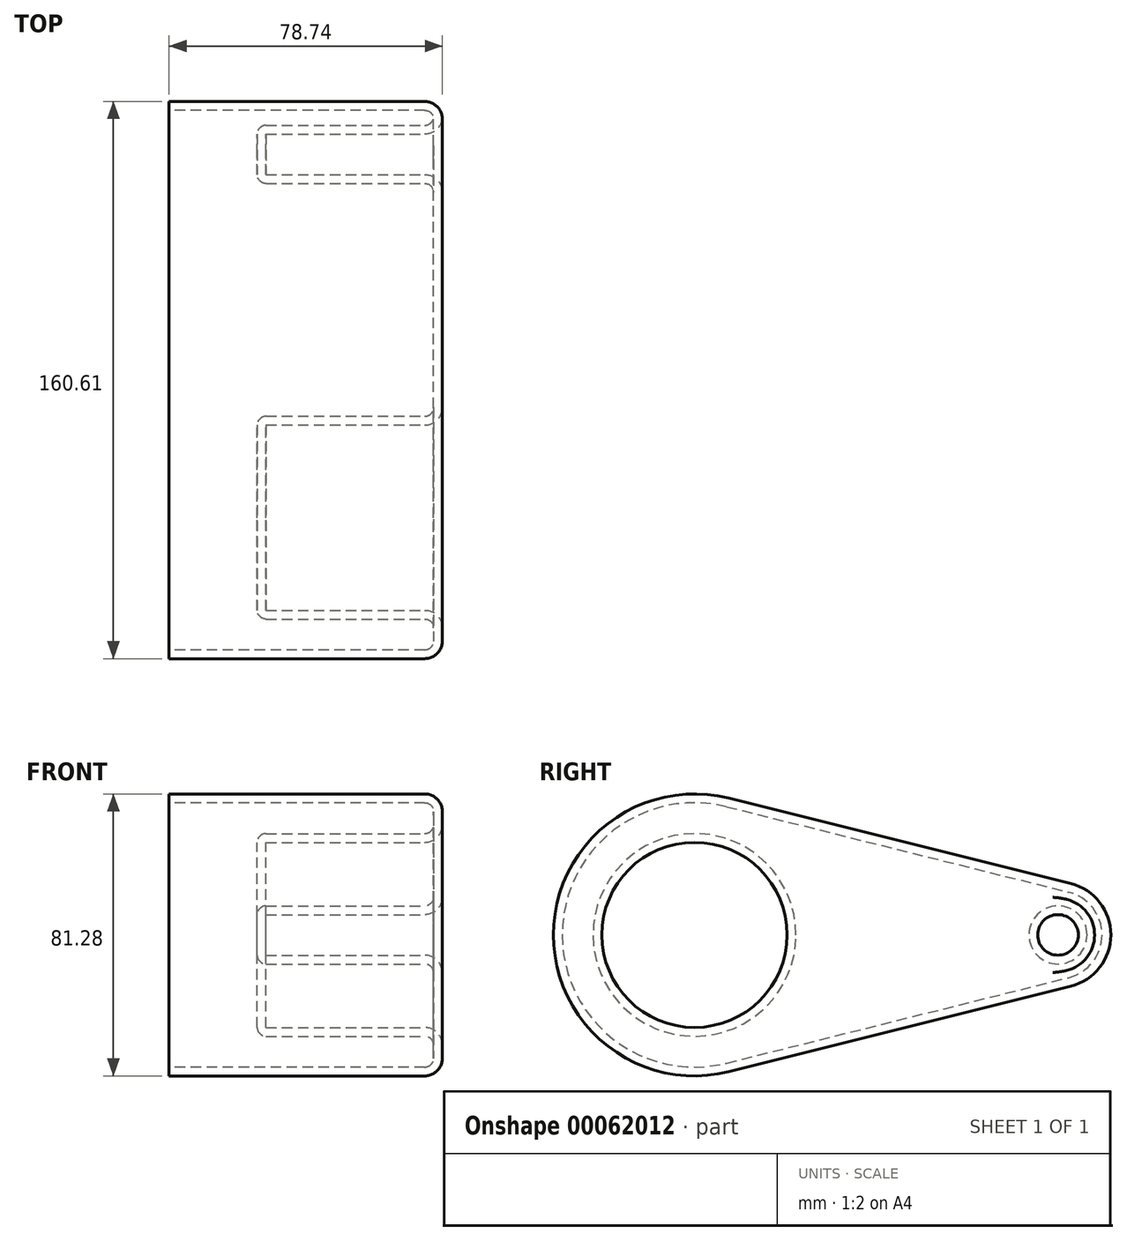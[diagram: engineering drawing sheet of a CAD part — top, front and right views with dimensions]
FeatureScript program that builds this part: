
annotation { "Feature Type Name" : "Feature", "Feature Type Description" : "" }
export const myFeature = defineFeature(function(context is Context, id is Id, definition is map)
    precondition{}
    {
        {
            var Q0;
            Q0=qCreatedBy(makeId("Right.planeOp"),FACE);
            var sketch = newSketch(context, id + "F3", { "sketchPlane" : qUnion([Q0])});
            skCircle(sketch, "E0", {"center": v(0, 0) * mm, "radius": 38.1 * mm});
            skCircle(sketch, "E1", {"center": v(104.73, 0) * mm, "radius": 12.7 * mm});
            skLineSegment(sketch, "E2", {"start": v(9.24, 36.96) * mm, "end": v(107.8, 12.32) * mm});
            skLineSegment(sketch, "E3", {"start": v(64.15, 21.02) * mm, "end": v(64.15, 21.02) * mm});
            skLineSegment(sketch, "E4", {"start": v(9.24, -36.96) * mm, "end": v(107.8, -12.32) * mm});
            skSolve(sketch);
        }
        {
            var Q0;
            Q0 = qSketchRegion(id + "F3", true);
            extrude(context, id + "F0", {"entities" : qUnion([Q0]), "depth" : 76.2 * mm});
        }
        {
            var Q0;
            Q0=makeQuery(id+"F0.opExtrude","CAP_FACE",FACE,{"disambiguationData":[OSD([sQuery(id+"F3.wireOp",EDGE,"E0"),sQuery(id+"F3.wireOp",EDGE,"E1"),sQuery(id+"F3.wireOp",EDGE,"E2"),sQuery(id+"F3.wireOp",EDGE,"E4")])],"isStart":false});
            var sketch = newSketch(context, id + "F4", { "sketchPlane" : qUnion([Q0])});
            skCircle(sketch, "E5", {"center": v(0, 0) * mm, "radius": 29.22 * mm});
            skCircle(sketch, "E6", {"center": v(104.73, 0) * mm, "radius": 8.38 * mm});
            skSolve(sketch);
        }
        {
            var Q0;
            Q0 = qSketchRegion(id + "F4", true);
            extrude(context, id + "F5", {"entities" : qUnion([Q0]), "operationType" : NewBodyOperationType.REMOVE, "oppositeDirection" : true, "depth" : 50.8 * mm});
        }
        {
            var Q0;
            Q0=makeQuery(id+"F0.opExtrude","CAP_FACE",FACE,{"disambiguationData":[OSD([sQuery(id+"F3.wireOp",EDGE,"E0"),sQuery(id+"F3.wireOp",EDGE,"E1"),sQuery(id+"F3.wireOp",EDGE,"E2"),sQuery(id+"F3.wireOp",EDGE,"E4")])],"isStart":false});
            var Q1;
            Q1=makeQuery(id+"F5.boolean.opBoolean","COPY",FACE,{"derivedFrom":makeQuery(id+"F5.opExtrude","CAP_FACE",FACE,{"disambiguationData":[OSD([sQuery(id+"F4.wireOp",EDGE,"E5")])],"isStart":false})});
            var Q2;
            Q2=makeQuery(id+"F5.boolean.opBoolean","COPY",FACE,{"derivedFrom":makeQuery(id+"F5.opExtrude","CAP_FACE",FACE,{"disambiguationData":[OSD([sQuery(id+"F4.wireOp",EDGE,"E6")])],"isStart":false})});
            fillet(context, id + "F1", {"entities" : qUnion([Q0, Q1, Q2]), "radius" : 2.54 * mm, "tangentPropagation" : true, "allowEdgeOverflow" : false});
        }
        {
            var Q0;
            Q0=makeQuery(id+"F0.opExtrude","CAP_FACE",FACE,{"disambiguationData":[OSD([sQuery(id+"F3.wireOp",EDGE,"E0"),sQuery(id+"F3.wireOp",EDGE,"E1"),sQuery(id+"F3.wireOp",EDGE,"E2"),sQuery(id+"F3.wireOp",EDGE,"E4")])],"isStart":true});
            shell(context, id + "F2", {"entities" : qUnion([Q0]), "thickness" : 2.54 * mm, "oppositeDirection" : true});
        }
    });
